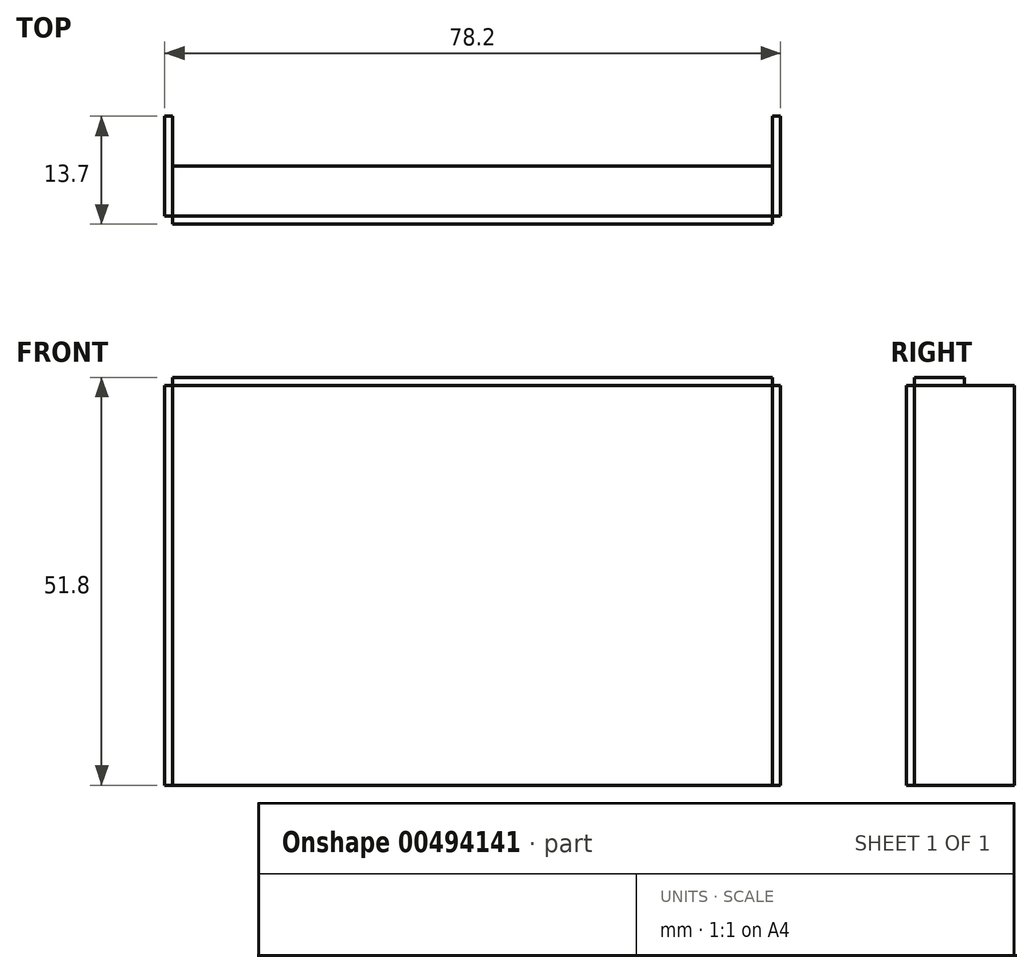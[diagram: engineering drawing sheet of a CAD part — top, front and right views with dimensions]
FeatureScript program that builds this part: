
annotation { "Feature Type Name" : "Feature", "Feature Type Description" : "" }
export const myFeature = defineFeature(function(context is Context, id is Id, definition is map)
    precondition{}
    {
        {
            var Q0;
            Q0=qCreatedBy(makeId("Front.planeOp"),FACE);
            var sketch = newSketch(context, id + "F0", { "sketchPlane" : qUnion([Q0])});
            skLineSegment(sketch, "E0.bottom", {"start": v(-48.34, 24.16) * mm, "end": v(27.86, 24.16) * mm});
            skLineSegment(sketch, "E0.top", {"start": v(-48.34, -26.64) * mm, "end": v(27.86, -26.64) * mm});
            skLineSegment(sketch, "E0.left", {"start": v(-48.34, 24.16) * mm, "end": v(-48.34, -26.64) * mm});
            skLineSegment(sketch, "E0.right", {"start": v(27.86, 24.16) * mm, "end": v(27.86, -26.64) * mm});
            skSolve(sketch);
        }
        {
            var Q0;
            Q0 = qSketchRegion(id + "F0", true);
            extrude(context, id + "F1", {"entities" : qUnion([Q0]), "depth" : 1 * mm});
        }
        {
            var Q0;
            Q0=makeQuery(id+"F1.opExtrude","SWEPT_FACE",FACE,{"disambiguationData":[OSD([sQuery(id+"F0.wireOp",EDGE,"E0.right")])]});
            var sketch = newSketch(context, id + "F2", { "sketchPlane" : qUnion([Q0])});
            skLineSegment(sketch, "E1.bottom", {"start": v(0, 24.16) * mm, "end": v(12.7, 24.16) * mm});
            skLineSegment(sketch, "E1.top", {"start": v(0, -26.64) * mm, "end": v(12.7, -26.64) * mm});
            skLineSegment(sketch, "E1.left", {"start": v(0, 24.16) * mm, "end": v(0, -26.64) * mm});
            skLineSegment(sketch, "E1.right", {"start": v(12.7, 24.16) * mm, "end": v(12.7, -26.64) * mm});
            skSolve(sketch);
        }
        {
            var Q0;
            Q0 = qSketchRegion(id + "F2", true);
            extrude(context, id + "F3", {"entities" : qUnion([Q0]), "depth" : 1 * mm});
        }
        {
            var Q0;
            Q0=makeQuery(id+"F1.opExtrude","SWEPT_FACE",FACE,{"disambiguationData":[OSD([sQuery(id+"F0.wireOp",EDGE,"E0.left")])]});
            var sketch = newSketch(context, id + "F4", { "sketchPlane" : qUnion([Q0])});
            skLineSegment(sketch, "E2.bottom", {"start": v(0, 24.16) * mm, "end": v(-12.7, 24.16) * mm});
            skLineSegment(sketch, "E2.top", {"start": v(0, -26.64) * mm, "end": v(-12.7, -26.64) * mm});
            skLineSegment(sketch, "E2.left", {"start": v(0, 24.16) * mm, "end": v(0, -26.64) * mm});
            skLineSegment(sketch, "E2.right", {"start": v(-12.7, 24.16) * mm, "end": v(-12.7, -26.64) * mm});
            skSolve(sketch);
        }
        {
            var Q0;
            Q0 = qSketchRegion(id + "F4", true);
            extrude(context, id + "F5", {"entities" : qUnion([Q0]), "depth" : 1 * mm});
        }
        {
            var Q0;
            Q0=makeQuery(id+"F1.opExtrude","SWEPT_FACE",FACE,{"disambiguationData":[OSD([sQuery(id+"F0.wireOp",EDGE,"E0.bottom")])]});
            var sketch = newSketch(context, id + "F6", { "sketchPlane" : qUnion([Q0])});
            skLineSegment(sketch, "E3.bottom", {"start": v(27.86, 0) * mm, "end": v(-48.34, 0) * mm});
            skLineSegment(sketch, "E3.top", {"start": v(27.86, 6.35) * mm, "end": v(-48.34, 6.35) * mm});
            skLineSegment(sketch, "E3.left", {"start": v(27.86, 0) * mm, "end": v(27.86, 6.35) * mm});
            skLineSegment(sketch, "E3.right", {"start": v(-48.34, 0) * mm, "end": v(-48.34, 6.35) * mm});
            skSolve(sketch);
        }
        {
            var Q0;
            Q0 = qSketchRegion(id + "F6", true);
            extrude(context, id + "F7", {"entities" : qUnion([Q0]), "depth" : 1 * mm});
        }
    });
